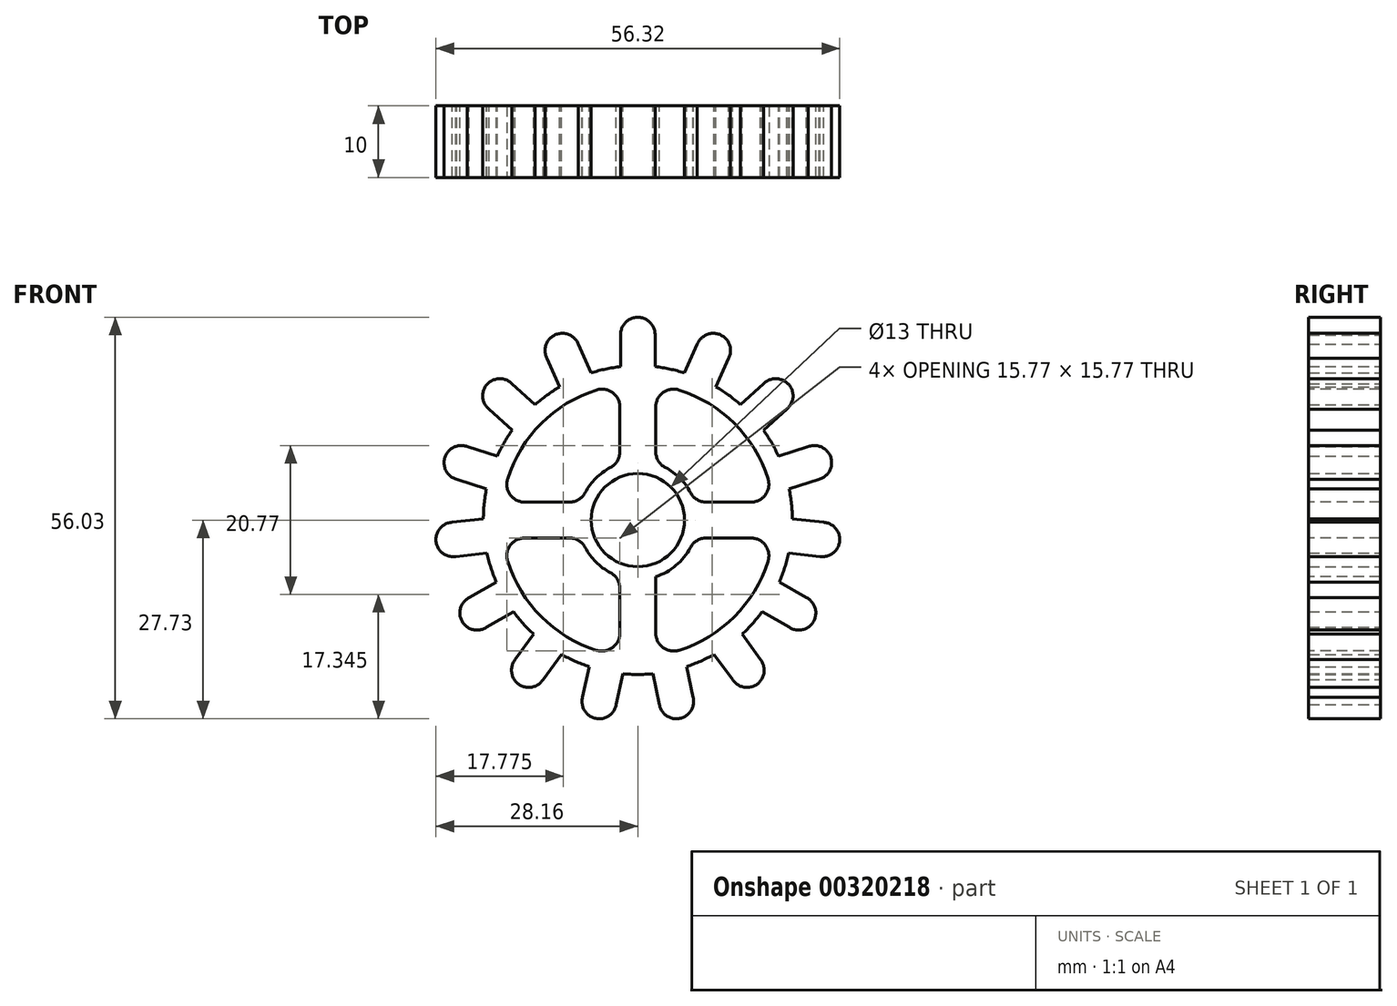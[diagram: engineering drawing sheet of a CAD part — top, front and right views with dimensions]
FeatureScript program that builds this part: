
annotation { "Feature Type Name" : "Feature", "Feature Type Description" : "" }
export const myFeature = defineFeature(function(context is Context, id is Id, definition is map)
    precondition{}
    {
        {
            var Q0;
            Q0=qCreatedBy(makeId("Front.planeOp"),FACE);
            var sketch = newSketch(context, id + "F0", { "sketchPlane" : qUnion([Q0])});
            skCircle(sketch, "E0", {"center": v(0, 0) * mm, "radius": 6.5 * mm});
            skArc(sketch, "E1", {"start": v(-10.9, 18.59) * mm, "mid": v(-12.67, 17.43) * mm, "end": v(-14.31, 16.11) * mm});
            skArc(sketch, "E2", {"start": v(2.4, 25.79) * mm, "mid": v(0, 28.3) * mm, "end": v(-2.4, 25.79) * mm});
            skLineSegment(sketch, "E3", {"start": v(2.4, 25.79) * mm, "end": v(2.4, 21.42) * mm});
            skLineSegment(sketch, "E4", {"start": v(-2.4, 25.79) * mm, "end": v(-2.4, 21.42) * mm});
            skLineSegment(sketch, "E5.1.0", {"start": v(-8.3, 24.53) * mm, "end": v(-6.52, 20.54) * mm});
            skArc(sketch, "E5.1.1", {"start": v(-8.3, 24.53) * mm, "mid": v(-11.51, 25.85) * mm, "end": v(-12.68, 22.58) * mm});
            skLineSegment(sketch, "E5.1.2", {"start": v(-12.68, 22.58) * mm, "end": v(-10.9, 18.59) * mm});
            skLineSegment(sketch, "E5.2.0", {"start": v(-17.56, 19.04) * mm, "end": v(-14.31, 16.11) * mm});
            skArc(sketch, "E5.2.1", {"start": v(-17.56, 19.04) * mm, "mid": v(-21.03, 18.94) * mm, "end": v(-20.77, 15.47) * mm});
            skLineSegment(sketch, "E5.2.2", {"start": v(-20.77, 15.47) * mm, "end": v(-17.52, 12.55) * mm});
            skLineSegment(sketch, "E5.3.0", {"start": v(-23.79, 10.25) * mm, "end": v(-19.63, 8.9) * mm});
            skArc(sketch, "E5.3.1", {"start": v(-23.79, 10.25) * mm, "mid": v(-26.91, 8.75) * mm, "end": v(-25.27, 5.69) * mm});
            skLineSegment(sketch, "E5.3.2", {"start": v(-25.27, 5.69) * mm, "end": v(-21.1, 4.34) * mm});
            skLineSegment(sketch, "E5.4.0", {"start": v(-25.9, -0.31) * mm, "end": v(-21.55, 0.15) * mm});
            skArc(sketch, "E5.4.1", {"start": v(-25.9, -0.31) * mm, "mid": v(-28.14, -2.96) * mm, "end": v(-25.4, -5.08) * mm});
            skLineSegment(sketch, "E5.4.2", {"start": v(-25.4, -5.08) * mm, "end": v(-21.05, -4.62) * mm});
            skLineSegment(sketch, "E5.5.0", {"start": v(-23.53, -10.82) * mm, "end": v(-19.75, -8.63) * mm});
            skArc(sketch, "E5.5.1", {"start": v(-23.53, -10.82) * mm, "mid": v(-24.5, -14.15) * mm, "end": v(-21.14, -14.97) * mm});
            skLineSegment(sketch, "E5.5.2", {"start": v(-21.14, -14.97) * mm, "end": v(-17.35, -12.78) * mm});
            skLineSegment(sketch, "E5.6.0", {"start": v(-17.1, -19.45) * mm, "end": v(-14.53, -15.92) * mm});
            skArc(sketch, "E5.6.1", {"start": v(-17.1, -19.45) * mm, "mid": v(-16.63, -22.9) * mm, "end": v(-13.22, -22.27) * mm});
            skLineSegment(sketch, "E5.6.2", {"start": v(-13.22, -22.27) * mm, "end": v(-10.65, -18.74) * mm});
            skLineSegment(sketch, "E5.7.0", {"start": v(-7.7, -24.73) * mm, "end": v(-6.8, -20.45) * mm});
            skArc(sketch, "E5.7.1", {"start": v(-7.7, -24.73) * mm, "mid": v(-5.88, -27.68) * mm, "end": v(-3.02, -25.72) * mm});
            skLineSegment(sketch, "E5.7.2", {"start": v(-3.02, -25.72) * mm, "end": v(-2.1, -21.45) * mm});
            skLineSegment(sketch, "E5.8.0", {"start": v(3.02, -25.72) * mm, "end": v(2.1, -21.45) * mm});
            skArc(sketch, "E5.8.1", {"start": v(3.02, -25.72) * mm, "mid": v(5.88, -27.68) * mm, "end": v(7.7, -24.73) * mm});
            skLineSegment(sketch, "E5.8.2", {"start": v(7.7, -24.73) * mm, "end": v(6.8, -20.45) * mm});
            skLineSegment(sketch, "E5.9.0", {"start": v(13.22, -22.27) * mm, "end": v(10.65, -18.74) * mm});
            skArc(sketch, "E5.9.1", {"start": v(13.22, -22.27) * mm, "mid": v(16.63, -22.9) * mm, "end": v(17.1, -19.45) * mm});
            skLineSegment(sketch, "E5.9.2", {"start": v(17.1, -19.45) * mm, "end": v(14.53, -15.92) * mm});
            skLineSegment(sketch, "E5.10.0", {"start": v(21.14, -14.97) * mm, "end": v(17.35, -12.78) * mm});
            skArc(sketch, "E5.10.1", {"start": v(21.14, -14.97) * mm, "mid": v(24.5, -14.15) * mm, "end": v(23.53, -10.82) * mm});
            skLineSegment(sketch, "E5.10.2", {"start": v(23.53, -10.82) * mm, "end": v(19.75, -8.63) * mm});
            skLineSegment(sketch, "E5.11.0", {"start": v(25.4, -5.08) * mm, "end": v(21.05, -4.62) * mm});
            skArc(sketch, "E5.11.1", {"start": v(25.4, -5.08) * mm, "mid": v(28.14, -2.96) * mm, "end": v(25.9, -0.31) * mm});
            skLineSegment(sketch, "E5.11.2", {"start": v(25.9, -0.31) * mm, "end": v(21.55, 0.15) * mm});
            skLineSegment(sketch, "E5.12.0", {"start": v(25.27, 5.69) * mm, "end": v(21.1, 4.34) * mm});
            skArc(sketch, "E5.12.1", {"start": v(25.27, 5.69) * mm, "mid": v(26.91, 8.75) * mm, "end": v(23.79, 10.25) * mm});
            skLineSegment(sketch, "E5.12.2", {"start": v(23.79, 10.25) * mm, "end": v(19.63, 8.9) * mm});
            skLineSegment(sketch, "E5.13.0", {"start": v(20.77, 15.47) * mm, "end": v(17.52, 12.55) * mm});
            skArc(sketch, "E5.13.1", {"start": v(20.77, 15.47) * mm, "mid": v(21.03, 18.94) * mm, "end": v(17.56, 19.04) * mm});
            skLineSegment(sketch, "E5.13.2", {"start": v(17.56, 19.04) * mm, "end": v(14.31, 16.11) * mm});
            skLineSegment(sketch, "E5.14.0", {"start": v(12.68, 22.58) * mm, "end": v(10.9, 18.59) * mm});
            skArc(sketch, "E5.14.1", {"start": v(12.68, 22.58) * mm, "mid": v(11.51, 25.85) * mm, "end": v(8.3, 24.53) * mm});
            skLineSegment(sketch, "E5.14.2", {"start": v(8.3, 24.53) * mm, "end": v(6.52, 20.54) * mm});
            skArc(sketch, "E6.trimOffspring", {"start": v(-17.52, 12.55) * mm, "mid": v(-18.66, 10.78) * mm, "end": v(-19.63, 8.9) * mm});
            skArc(sketch, "E7.trimOffspring", {"start": v(-21.1, 4.34) * mm, "mid": v(-21.43, 2.25) * mm, "end": v(-21.55, 0.15) * mm});
            skArc(sketch, "E8.trimOffspring", {"start": v(-21.05, -4.62) * mm, "mid": v(-20.5, -6.66) * mm, "end": v(-19.75, -8.63) * mm});
            skArc(sketch, "E9.trimOffspring", {"start": v(-17.35, -12.78) * mm, "mid": v(-16.01, -14.42) * mm, "end": v(-14.53, -15.92) * mm});
            skArc(sketch, "E10.trimOffspring", {"start": v(-10.65, -18.74) * mm, "mid": v(-8.77, -19.69) * mm, "end": v(-6.8, -20.45) * mm});
            skArc(sketch, "E11.trimOffspring", {"start": v(-2.1, -21.45) * mm, "mid": v(0, -21.55) * mm, "end": v(2.1, -21.45) * mm});
            skArc(sketch, "E12.trimOffspring", {"start": v(6.8, -20.45) * mm, "mid": v(8.77, -19.69) * mm, "end": v(10.65, -18.74) * mm});
            skArc(sketch, "E13.trimOffspring", {"start": v(14.53, -15.92) * mm, "mid": v(16.01, -14.42) * mm, "end": v(17.35, -12.78) * mm});
            skArc(sketch, "E14.trimOffspring", {"start": v(19.75, -8.63) * mm, "mid": v(20.5, -6.66) * mm, "end": v(21.05, -4.62) * mm});
            skArc(sketch, "E15.trimOffspring", {"start": v(21.55, 0.15) * mm, "mid": v(21.43, 2.25) * mm, "end": v(21.1, 4.34) * mm});
            skArc(sketch, "E16.trimOffspring", {"start": v(19.63, 8.9) * mm, "mid": v(18.66, 10.78) * mm, "end": v(17.52, 12.55) * mm});
            skArc(sketch, "E17.trimOffspring", {"start": v(14.31, 16.11) * mm, "mid": v(12.67, 17.43) * mm, "end": v(10.9, 18.59) * mm});
            skArc(sketch, "E18.trimOffspring", {"start": v(6.52, 20.54) * mm, "mid": v(4.48, 21.08) * mm, "end": v(2.4, 21.42) * mm});
            skArc(sketch, "E19.trimOffspring", {"start": v(-2.4, 21.42) * mm, "mid": v(-4.48, 21.08) * mm, "end": v(-6.52, 20.54) * mm});
            skSolve(sketch);
        }
        {
            var Q0;
            Q0=qSketchRegion(id+"F0",true);
            extrude(context, id + "F1", {"entities" : qUnion([Q0]), "endBound" : BoundingType.SYMMETRIC, "depth" : 10 * mm});
        }
        {
            var Q0;
            Q0=makeQuery(id+"F1.opExtrude","CAP_FACE",FACE,{"disambiguationData":[OSD([sQuery(id+"F0.wireOp",EDGE,"E0"),sQuery(id+"F0.wireOp",EDGE,"E1"),sQuery(id+"F0.wireOp",EDGE,"E2"),sQuery(id+"F0.wireOp",EDGE,"E3"),sQuery(id+"F0.wireOp",EDGE,"E4"),sQuery(id+"F0.wireOp",EDGE,"E5.1.0"),sQuery(id+"F0.wireOp",EDGE,"E5.1.1"),sQuery(id+"F0.wireOp",EDGE,"E5.1.2"),sQuery(id+"F0.wireOp",EDGE,"E5.2.0"),sQuery(id+"F0.wireOp",EDGE,"E5.2.1"),sQuery(id+"F0.wireOp",EDGE,"E5.2.2"),sQuery(id+"F0.wireOp",EDGE,"E5.3.0"),sQuery(id+"F0.wireOp",EDGE,"E5.3.1"),sQuery(id+"F0.wireOp",EDGE,"E5.3.2"),sQuery(id+"F0.wireOp",EDGE,"E5.4.0"),sQuery(id+"F0.wireOp",EDGE,"E5.4.1"),sQuery(id+"F0.wireOp",EDGE,"E5.4.2"),sQuery(id+"F0.wireOp",EDGE,"E5.5.0"),sQuery(id+"F0.wireOp",EDGE,"E5.5.1"),sQuery(id+"F0.wireOp",EDGE,"E5.5.2"),sQuery(id+"F0.wireOp",EDGE,"E5.6.0"),sQuery(id+"F0.wireOp",EDGE,"E5.6.1"),sQuery(id+"F0.wireOp",EDGE,"E5.6.2"),sQuery(id+"F0.wireOp",EDGE,"E5.7.0"),sQuery(id+"F0.wireOp",EDGE,"E5.7.1"),sQuery(id+"F0.wireOp",EDGE,"E5.7.2"),sQuery(id+"F0.wireOp",EDGE,"E5.8.0"),sQuery(id+"F0.wireOp",EDGE,"E5.8.1"),sQuery(id+"F0.wireOp",EDGE,"E5.8.2"),sQuery(id+"F0.wireOp",EDGE,"E5.9.0"),sQuery(id+"F0.wireOp",EDGE,"E5.9.1"),sQuery(id+"F0.wireOp",EDGE,"E5.9.2"),sQuery(id+"F0.wireOp",EDGE,"E5.10.0"),sQuery(id+"F0.wireOp",EDGE,"E5.10.1"),sQuery(id+"F0.wireOp",EDGE,"E5.10.2"),sQuery(id+"F0.wireOp",EDGE,"E5.11.0"),sQuery(id+"F0.wireOp",EDGE,"E5.11.1"),sQuery(id+"F0.wireOp",EDGE,"E5.11.2"),sQuery(id+"F0.wireOp",EDGE,"E5.12.0"),sQuery(id+"F0.wireOp",EDGE,"E5.12.1"),sQuery(id+"F0.wireOp",EDGE,"E5.12.2"),sQuery(id+"F0.wireOp",EDGE,"E5.13.0"),sQuery(id+"F0.wireOp",EDGE,"E5.13.1"),sQuery(id+"F0.wireOp",EDGE,"E5.13.2"),sQuery(id+"F0.wireOp",EDGE,"E5.14.0"),sQuery(id+"F0.wireOp",EDGE,"E5.14.1"),sQuery(id+"F0.wireOp",EDGE,"E5.14.2"),sQuery(id+"F0.wireOp",EDGE,"E6.trimOffspring"),sQuery(id+"F0.wireOp",EDGE,"E7.trimOffspring"),sQuery(id+"F0.wireOp",EDGE,"E8.trimOffspring"),sQuery(id+"F0.wireOp",EDGE,"E9.trimOffspring"),sQuery(id+"F0.wireOp",EDGE,"E10.trimOffspring"),sQuery(id+"F0.wireOp",EDGE,"E11.trimOffspring"),sQuery(id+"F0.wireOp",EDGE,"E12.trimOffspring"),sQuery(id+"F0.wireOp",EDGE,"E13.trimOffspring"),sQuery(id+"F0.wireOp",EDGE,"E14.trimOffspring"),sQuery(id+"F0.wireOp",EDGE,"E15.trimOffspring"),sQuery(id+"F0.wireOp",EDGE,"E16.trimOffspring"),sQuery(id+"F0.wireOp",EDGE,"E17.trimOffspring"),sQuery(id+"F0.wireOp",EDGE,"E18.trimOffspring"),sQuery(id+"F0.wireOp",EDGE,"E19.trimOffspring")])],"isStart":false});
            var sketch = newSketch(context, id + "F2", { "sketchPlane" : qUnion([Q0])});
            skArc(sketch, "E20", {"start": v(-18.16, 5.76) * mm, "mid": v(-13.47, 13.47) * mm, "end": v(-5.76, 18.16) * mm});
            skLineSegment(sketch, "E21", {"start": v(0, 0) * mm, "end": v(0, 23.63) * mm, "construction": true});
            skLineSegment(sketch, "E22", {"start": v(0, 23.63) * mm, "end": v(0, 19.05) * mm, "construction": true});
            skLineSegment(sketch, "E23", {"start": v(0, 0) * mm, "end": v(-36.4, 0) * mm, "construction": true});
            skLineSegment(sketch, "E24", {"start": v(-2.5, 15.78) * mm, "end": v(-2.5, 9.55) * mm});
            skLineSegment(sketch, "E25", {"start": v(-15.78, 2.5) * mm, "end": v(-9.55, 2.5) * mm});
            skPoint(sketch, "E26.orphan", {"position": v(0, 19.05) * mm});
            skPoint(sketch, "E27.orphan", {"position": v(-19.05, 0) * mm});
            skPoint(sketch, "E28.visualSharp", {"position": v(-2.5, 18.89) * mm});
            skArc(sketch, "E28.filletArc", {"start": v(-2.5, 15.78) * mm, "mid": v(-3.52, 17.8) * mm, "end": v(-5.76, 18.16) * mm});
            skPoint(sketch, "E29.visualSharp", {"position": v(-18.89, 2.5) * mm});
            skArc(sketch, "E29.filletArc", {"start": v(-18.16, 5.76) * mm, "mid": v(-17.8, 3.52) * mm, "end": v(-15.78, 2.5) * mm});
            skPoint(sketch, "E30.visualSharp", {"position": v(-6, 2.5) * mm});
            skPoint(sketch, "E31.visualSharp", {"position": v(-2.5, 6) * mm});
            skArc(sketch, "E32.MirrorCS", {"start": v(2.5, 15.78) * mm, "mid": v(3.52, 17.8) * mm, "end": v(5.76, 18.16) * mm});
            skArc(sketch, "E33.MirrorCS", {"start": v(18.16, 5.76) * mm, "mid": v(13.47, 13.47) * mm, "end": v(5.76, 18.16) * mm});
            skArc(sketch, "E34.MirrorCS", {"start": v(18.16, 5.76) * mm, "mid": v(17.8, 3.52) * mm, "end": v(15.78, 2.5) * mm});
            skLineSegment(sketch, "E35.MirrorCS", {"start": v(15.78, 2.5) * mm, "end": v(9.55, 2.5) * mm});
            skLineSegment(sketch, "E36.MirrorCS", {"start": v(2.5, 15.78) * mm, "end": v(2.5, 9.55) * mm});
            skLineSegment(sketch, "E37.MirrorCS", {"start": v(-15.78, -2.5) * mm, "end": v(-9.55, -2.5) * mm});
            skArc(sketch, "E38.MirrorCS", {"start": v(-18.16, -5.76) * mm, "mid": v(-17.8, -3.52) * mm, "end": v(-15.78, -2.5) * mm});
            skArc(sketch, "E39.MirrorCS", {"start": v(-18.16, -5.76) * mm, "mid": v(-13.47, -13.47) * mm, "end": v(-5.76, -18.16) * mm});
            skArc(sketch, "E40.MirrorCS", {"start": v(-2.5, -15.78) * mm, "mid": v(-3.52, -17.8) * mm, "end": v(-5.76, -18.16) * mm});
            skLineSegment(sketch, "E41.MirrorCS", {"start": v(-2.5, -15.78) * mm, "end": v(-2.5, -9.55) * mm});
            skPoint(sketch, "E42.MirrorP", {"position": v(-2.5, -6) * mm});
            skLineSegment(sketch, "E43.MirrorCS", {"start": v(2.5, -15.78) * mm, "end": v(2.5, -7.48) * mm});
            skArc(sketch, "E44.MirrorCS", {"start": v(2.5, -15.78) * mm, "mid": v(3.52, -17.8) * mm, "end": v(5.76, -18.16) * mm});
            skArc(sketch, "E45.MirrorCS", {"start": v(18.16, -5.76) * mm, "mid": v(13.47, -13.47) * mm, "end": v(5.76, -18.16) * mm});
            skArc(sketch, "E46.MirrorCS", {"start": v(18.16, -5.76) * mm, "mid": v(17.8, -3.52) * mm, "end": v(15.78, -2.5) * mm});
            skLineSegment(sketch, "E47.MirrorCS", {"start": v(15.78, -2.5) * mm, "end": v(9.55, -2.5) * mm});
            skLineSegment(sketch, "E48.trimOffspring", {"start": v(0, 5) * mm, "end": v(0, 0) * mm, "construction": true});
            skArc(sketch, "E49", {"start": v(2.5, -7.9) * mm, "mid": v(5.32, -6.34) * mm, "end": v(7.33, -3.84) * mm});
            skPoint(sketch, "E50.trimOffspring.end.orphan", {"position": v(-5.4, 3.61) * mm});
            skPoint(sketch, "E31.filletArc.start.orphan", {"position": v(-3.61, 5.4) * mm});
            skPoint(sketch, "E51.MirrorCS.end.orphan", {"position": v(2.5, 7.48) * mm});
            skPoint(sketch, "E51.MirrorCS.start.orphan", {"position": v(3.61, 5.4) * mm});
            skPoint(sketch, "E52.MirrorCS.end.orphan", {"position": v(5.4, 3.61) * mm});
            skPoint(sketch, "E53.MirrorCS.start.orphan", {"position": v(7.48, 2.5) * mm});
            skPoint(sketch, "E54.MirrorCS.end.orphan", {"position": v(5.4, -3.61) * mm});
            skPoint(sketch, "E54.MirrorCS.start.orphan", {"position": v(7.48, -2.5) * mm});
            skPoint(sketch, "E55.MirrorCS.start.orphan", {"position": v(3.61, -5.4) * mm});
            skPoint(sketch, "E56.MirrorCS.end.orphan", {"position": v(2.5, -7.48) * mm});
            skPoint(sketch, "E57.MirrorCS.end.orphan", {"position": v(-2.5, -7.48) * mm});
            skPoint(sketch, "E57.MirrorCS.start.orphan", {"position": v(-3.61, -5.4) * mm});
            skPoint(sketch, "E58.MirrorCS.end.orphan", {"position": v(-5.4, -3.61) * mm});
            skPoint(sketch, "E59.MirrorCS.start.orphan", {"position": v(-7.48, -2.5) * mm});
            skPoint(sketch, "E60.orphan", {"position": v(-7.48, 2.5) * mm});
            skArc(sketch, "E61.trimOffspring", {"start": v(7.33, 3.84) * mm, "mid": v(5.85, 5.85) * mm, "end": v(3.84, 7.33) * mm});
            skArc(sketch, "E62.trimOffspring", {"start": v(-3.84, 7.33) * mm, "mid": v(-5.85, 5.85) * mm, "end": v(-7.33, 3.84) * mm});
            skPoint(sketch, "E63.visualSharp", {"position": v(-2.5, -7.9) * mm});
            skArc(sketch, "E63.filletArc", {"start": v(-2.5, -9.55) * mm, "mid": v(-2.86, -8.25) * mm, "end": v(-3.84, -7.33) * mm});
            skArc(sketch, "E64.trimOffspring", {"start": v(-7.33, -3.84) * mm, "mid": v(-5.85, -5.85) * mm, "end": v(-3.84, -7.33) * mm});
            skPoint(sketch, "E65.visualSharp", {"position": v(-7.9, -2.5) * mm});
            skArc(sketch, "E65.filletArc", {"start": v(-7.33, -3.84) * mm, "mid": v(-8.25, -2.86) * mm, "end": v(-9.55, -2.5) * mm});
            skPoint(sketch, "E66.visualSharp", {"position": v(-7.9, 2.5) * mm});
            skArc(sketch, "E66.filletArc", {"start": v(-9.55, 2.5) * mm, "mid": v(-8.25, 2.86) * mm, "end": v(-7.33, 3.84) * mm});
            skPoint(sketch, "E67.orphan", {"position": v(-2.5, 7.48) * mm});
            skPoint(sketch, "E68.visualSharp", {"position": v(-2.5, 7.9) * mm});
            skArc(sketch, "E68.filletArc", {"start": v(-3.84, 7.33) * mm, "mid": v(-2.86, 8.25) * mm, "end": v(-2.5, 9.55) * mm});
            skPoint(sketch, "E69.visualSharp", {"position": v(2.5, 7.9) * mm});
            skArc(sketch, "E69.filletArc", {"start": v(2.5, 9.55) * mm, "mid": v(2.86, 8.25) * mm, "end": v(3.84, 7.33) * mm});
            skPoint(sketch, "E70.visualSharp", {"position": v(7.9, 2.5) * mm});
            skArc(sketch, "E70.filletArc", {"start": v(7.33, 3.84) * mm, "mid": v(8.25, 2.86) * mm, "end": v(9.55, 2.5) * mm});
            skPoint(sketch, "E71.visualSharp", {"position": v(7.9, -2.5) * mm});
            skArc(sketch, "E71.filletArc", {"start": v(9.55, -2.5) * mm, "mid": v(8.25, -2.86) * mm, "end": v(7.33, -3.84) * mm});
            skSolve(sketch);
        }
        {
            var Q0;
            Q0=qSketchRegion(id+"F2",true);
            extrude(context, id + "F3", {"entities" : qUnion([Q0]), "operationType" : NewBodyOperationType.REMOVE, "oppositeDirection" : true, "depth" : 10 * mm});
        }
    });
